# Revit family: IS_iLifeB_T5271_BIM_NL
name_source: partatom
category: Plumbing Fixtures
units: mm (PartAtom-declared; Revit-internal decimal feet)

## family parameters
Always vertical = No
Cut with Voids When Loaded = No
OmniClass Number = 23.45.05.14.21.11
OmniClass Title = Bath/Shower Units
Part Type = Normal
Room Calculation Point = No
Round Connector Dimension = Use Diameter
Shared = No
Work Plane-Based = No

## types (7) — shared parameters
Accessories = https://www.idealstandard.co.uk
Afmetingen = https://www.idealstandard.nl
AfstandsEenheid = Millimeter
AreaUnits = millimetres
Artikelomschrijving = I.LIFE B WASCHTISCHUNTERSCHRANK 1 SCHUBLADE 80CM
Artikelreferentie = I.LIFE B WASCHTISCHUNTERSCHRANK 1 SCHUBLADE 80CM
AssetType = Fixed
Auteur = Ideal Standard
BIMobject category = Storage
BIMobject category code = sanitary-storage
BIMobject main category = Sanitary
BIMobject main category code = sanitary
Beschrijvinggarantie = Herstellergarantie
Brand = Ideal Standard
Brand url = https://www.idealstandard.nl
Breedte = 800
Category = Sanitary
Classification = Furniture
CodePerformance = n /a
ComponentNames = n /a
ConnectionType = n /a
Constituents = n /a
CurrencyUnit = €
CurrentRevision = 1
Date of publishing = 09/09/2022
Description = I.LIFE B VANITY UNIT 1 DRAWER 80CM
Diepte = 525 mm
DurationUnit = Years
DuurEenheid = Jahre
Edition number = 1
ElementType = Fixed
Features = VANITY UNIT 1 DRAWER 80CM
Garantieonderdelen = 2
Garantieunits = Jahre
GemaaktOp = 09/09/2022
Help = https://www.idealstandard.nl
Hoogte = 450
Hulp = https://www.idealstandard.nl
IFC Classification = Furniture
IfcExportAs = IfcFurnitureType
IfcExportType = BATHROOMCABINET
Installatieinstructies = https://www.idealstandard.nl
Installation instructions = https://www.idealstandard.nl
InstallationInstructions = https://www.idealstandard.nl
Lengte = 525 mm
LinearUnits = Millimeter
MaintenanceInformation = https://www.idealstandard.nl
Manufacturer = Ideal Standard
Manufacturer name = Ideal Standard
ManufacturerURL = https://www.idealstandard.nl
Masterformat 2014 Code = 22 40 00
Masterformat 2014 Description = Plumbing Fixtures
Materiaal = Holz
Material = Wood
Material main = Wood
Merk = Ideal Standard
ModelReference = I.LIFE B VANITY UNIT 1 DRAWER 80CM
NBS Reference Code = 45-35-72/318
NBS Reference Description = Bathroom cabinets
NettWeight = 22.44 Kg
NominalDepth = 525 mm
NominalHeight = 450 mm  [stored 1.47638 ft]
NominalWidth = 800 mm  [stored 2.62467 ft]
OmniClass Code = 23.45.00.00
OmniClass Description = Sanitary Equipment
OppervlakteEenheid = Millimeter
PredefinedType = Sanitay Furniture
Product Guid = 238344a2-01c4-4ec0-8f47-99dd745c9348
Product SKU = T5271
Product certification = https://www.idealstandard.nl
Product data url = https://bimobject.com
Product family = I.life B
Product group = Bathroom Furniture
Product name = I.LIFE B VANITY UNIT 1 DRAWER 80CM
Product url = https://www.idealstandard.nl
ProductInformation = https://www.idealstandard.nl
Productinformatie = https://www.idealstandard.nl
QR code = http://bimobject.com
Revisie = 1
Shape = Rectangulard
Size = 800 x 525 x 450 mm
Space = Internal
SpareParts = https://www.idealstandard.nl
Technical description = https://www.idealstandard.nl
Telefoonnummer = 077 355 08 08
Type Comments = Plumbing
UNSPSC Code = 30181500
URL = https://www.idealstandard.nl
Uniclass 1.4 Code = L8241
Uniclass 1.4 Description = Bathroom cabinets
Uniclass 2.0 Code = Pr_40_30_78_06
Uniclass 2.0 Description = Bathroom Cabinets
Uniclass 2015 Code = Pr_40_30_87_03
Uniclass 2015 Name = Bathroom cabinets
Uniclass2015Beschrijving = Bathroom cabinets
Uniclass2015Code = Pr_40_30_87_03
Uniclass2015Referentie = Pr_40_30_87_03
Uniclass2015Title = Bathroom cabinets
Uniclass2015Version = v1.27
Uniformat II Code = E 2020
Uniformat II Description = Movable Furnishings
Urlproducent = https://www.idealstandard.nl
ValutaEenheid = Euro
Versie = 1
Version = 1
VolumeUnits = Litres
Volumeunits = Liter
Vorm = rechteckig
WRASURL = https://www.wrasapprovals.co.uk
WaarborgGarantieInstallatie = n /a
WarrantyDescription = manufacturer warranty
WarrantyDurationParts = 1
WarrantyDurationUnit = years
Weight Net (Kg) = 22.44
Wisselstukken = https://www.idealstandard.nl
Youtube clip = https://www.youtube.com
zero-valued in all types: BrutoGewicht, Nettogewicht, Vervangingskosten

## per-type parameters (varying)
| type | Afwerking | Artikelnummer | BIMObjectName | BarCode | Barcode | BimObjectNaam | Color | Finish | GTIN code | Kleur | MainColor | Model | ModelNumber | Name |
| T5271DU - I.LIFE B VANITY UNIT 1 DRAWER 80CM - WHITE MATT | weiß matt | T5271DU | IS_IdealStandard_BathroomCabinets_I.LifeB_BD408 | 8014140502395 | 8014140502395 | IS_IdealStandard_BathroomCabinets_I.LifeB_BD408 | weiß matt | white matt | 8014140502395 | weiß matt | weiß matt | T5271DU | T5271DU | BathroomCabinets_I.LifeB_BD408_IdealStandard |
| T5271NF - I.LIFE B VANITY UNIT 1 DRAWER 80CM - SAND BEIGE MATT | sandbeige matt | T5271NF | IS_IdealStandard_BathroomCabinets_I.LifeB_BD408 | 8014140494270 | 8014140494270 | IS_IdealStandard_BathroomCabinets_I.LifeB_BD408 | sandbeige matt | sand beige matt | 8014140494270 | sandbeige matt | sandbeige matt | T5271NF | T5271NF | BathroomCabinets_I.LifeB_BD408_IdealStandard |
| T5271NG - I.LIFE B VANITY UNIT 1 DRAWER 80CM - QUARTZ GREY MATT | quarzgrau matt | T5271NG | IS_IdealStandard_BathroomCabinets_I.LifeB_BD408 | 8014140494287 | 8014140494287 | IS_IdealStandard_BathroomCabinets_I.LifeB_BD408 | quarzgrau matt | quartz grey matt | 8014140494287 | quarzgrau matt | quarzgrau matt | T5271NG | T5271NG | BathroomCabinets_I.LifeB_BD408_IdealStandard |
| T5271NH - I.LIFE B VANITY UNIT 1 DRAWER 80CM - GREIGE MATT | grau matt | T5271NH | IS_IdealStandard_BathroomCabinets_I.LifeB_BD408 | 8014140494294 | 8014140494294 | IS_IdealStandard_BathroomCabinets_I.LifeB_BD408 | grau matt | greige matt | 8014140494294 | grau matt | grau matt | T5271NH | T5271NH | BathroomCabinets_I.LifeB_BD408_IdealStandard |
| T5271NX - I.LIFE B VANITY UNIT 1 DRAWER 80CM - NATURAL OAK | natürliche Eiche | T5271NX | IS_IdealStandard_BathroomCabinets_I.LifeB_BD408 | 8014140502418 | 8014140502418 | IS_IdealStandard_BathroomCabinets_I.LifeB_BD408 | natürliche Eiche | natural oak | 8014140502418 | natürliche Eiche | natürliche Eiche | T5271NX | T5271NX | BathroomCabinets_I.LifeB_BD408_IdealStandard |
| T5271NW - I.LIFE B VANITY UNIT 1 DRAWER 80CM - COFFEE OAK | Kaffee Eiche | T5271NW | IS_IdealStandard_BathroomCabinets_I.LifeB_BD409 | 8014140502401 | 8014140502401 | IS_IdealStandard_BathroomCabinets_I.LifeB_BD409 | Kaffee Eiche | coffee oak | 8014140502401 | Kaffee Eiche | Kaffee Eiche | T5271NW | T5271NW | BathroomCabinets_I.LifeB_BD409_IdealStandard |
| T5271NV - I.LIFE B VANITY UNIT 1 DRAWER 80CM - CARBON GREY MATT | carbongrau matt | T5271NV | IS_IdealStandard_BathroomCabinets_I.LifeB_BD410 | 8014140494300 | 8014140494300 | IS_IdealStandard_BathroomCabinets_I.LifeB_BD410 | carbongrau matt | carbon grey matt | 8014140494300 | carbongrau matt | carbongrau matt | T5271NV | T5271NV | BathroomCabinets_I.LifeB_BD410_IdealStandard |

note: [stored X ft] marks values corroborated as IEEE doubles in the binary element streams (Revit-internal decimal feet)

## geometry (parser evidence)
native form markers: Sweep x1
no freeform markers — native parametric forms only
